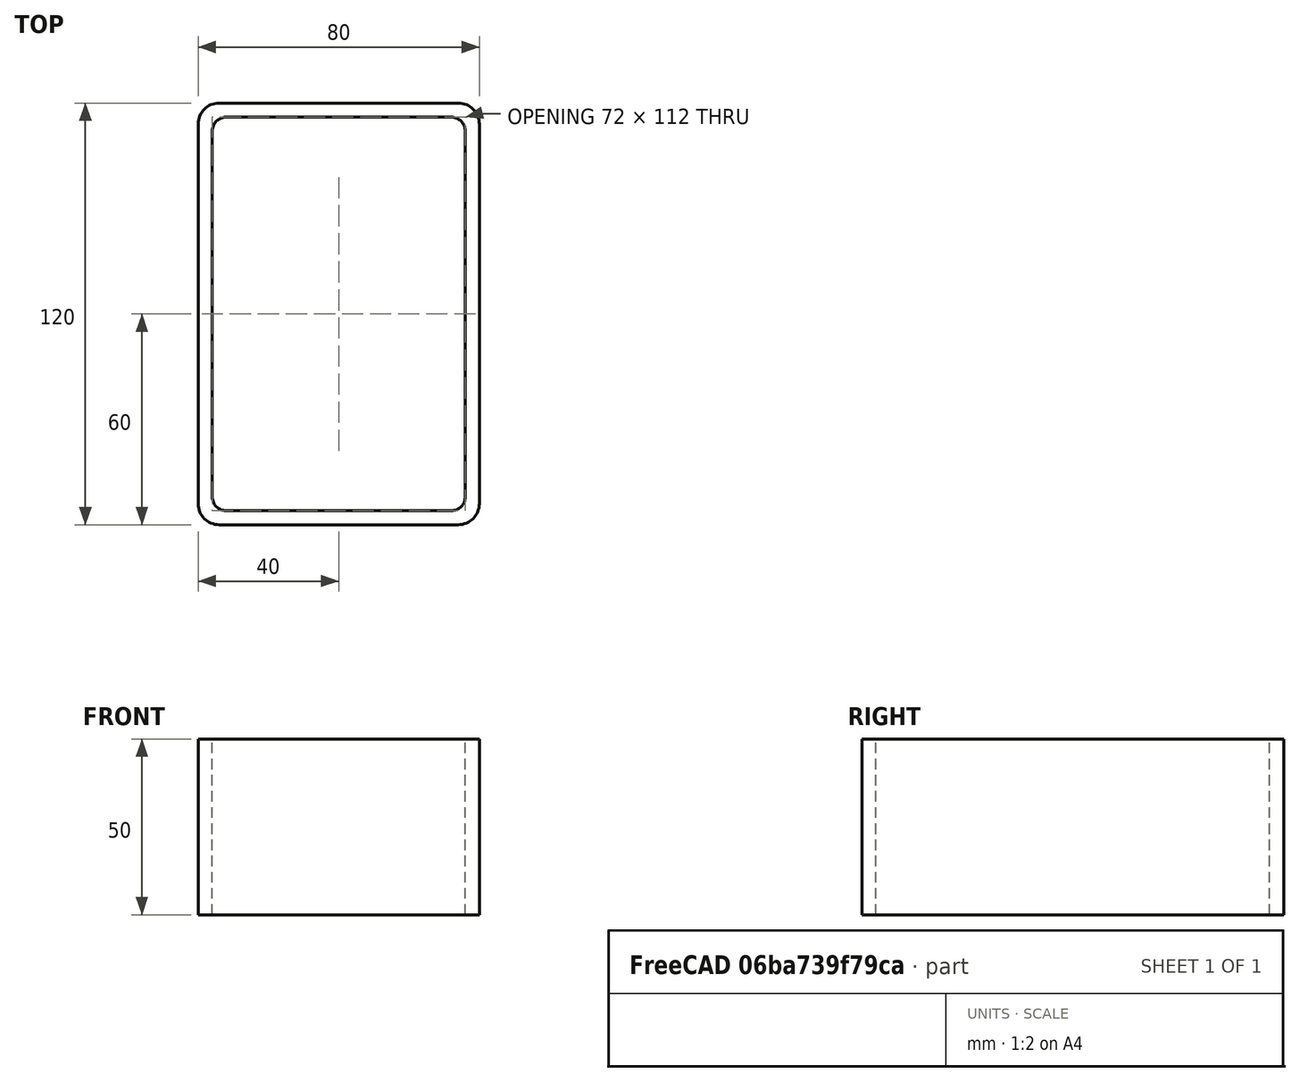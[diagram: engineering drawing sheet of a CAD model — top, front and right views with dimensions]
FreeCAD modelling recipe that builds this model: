
FCSTD DOCUMENT  (FreeCAD 0.15R4671 (Git))
Label: Rectangular hollow section 120x80x4 EN10219 S235JRH
License: All rights reserved
LicenseURL: http://en.wikipedia.org/wiki/All_rights_reserved
objects: Sketcher::SketchObject×1, Part::Extrusion×1
note: 2 computed .brp shape members not serialized (recipe doc carries the construction recipe); baked Part::Feature solids carry a one-line shape summary decoded from their .brp

FEATURE [Sketcher::SketchObject] Sketch
  sketch-geometry (16):
    g0: LineSegment StartX=-32 StartY=56 StartZ=0 EndX=32 EndY=56 EndZ=0
    g1: LineSegment StartX=36 StartY=52 StartZ=0 EndX=36 EndY=-52 EndZ=0
    g2: LineSegment StartX=32 StartY=-56 StartZ=0 EndX=-32 EndY=-56 EndZ=0
    g3: LineSegment StartX=-36 StartY=-52 StartZ=0 EndX=-36 EndY=52 EndZ=0
    g4: LineSegment StartX=-34 StartY=60 StartZ=0 EndX=34 EndY=60 EndZ=0
    g5: LineSegment StartX=40 StartY=54 StartZ=0 EndX=40 EndY=-54 EndZ=0
    g6: LineSegment StartX=34 StartY=-60 StartZ=0 EndX=-34 EndY=-60 EndZ=0
    g7: LineSegment StartX=-40 StartY=-54 StartZ=0 EndX=-40 EndY=54 EndZ=0
    g8: ArcOfCircle CenterX=-32 CenterY=52 CenterZ=0 NormalX=0 NormalY=0 NormalZ=1 Radius=4 StartAngle=1.5708 EndAngle=3.14159
    g9: ArcOfCircle CenterX=32 CenterY=52 CenterZ=0 NormalX=0 NormalY=0 NormalZ=1 Radius=4 StartAngle=0 EndAngle=1.5708
    g10: ArcOfCircle CenterX=32 CenterY=-52 CenterZ=0 NormalX=0 NormalY=0 NormalZ=1 Radius=4 StartAngle=4.71239 EndAngle=6.28319
    g11: ArcOfCircle CenterX=-32 CenterY=-52 CenterZ=0 NormalX=0 NormalY=0 NormalZ=1 Radius=4 StartAngle=3.14159 EndAngle=4.71239
    g12: ArcOfCircle CenterX=34 CenterY=54 CenterZ=0 NormalX=0 NormalY=0 NormalZ=1 Radius=6 StartAngle=0 EndAngle=1.5708
    g13: ArcOfCircle CenterX=34 CenterY=-54 CenterZ=0 NormalX=0 NormalY=0 NormalZ=1 Radius=6 StartAngle=4.71239 EndAngle=6.28319
    g14: ArcOfCircle CenterX=-34 CenterY=-54 CenterZ=0 NormalX=0 NormalY=0 NormalZ=1 Radius=6 StartAngle=3.14159 EndAngle=4.71239
    g15: ArcOfCircle CenterX=-34 CenterY=54 CenterZ=0 NormalX=0 NormalY=0 NormalZ=1 Radius=6 StartAngle=1.5708 EndAngle=3.14159
  constraints (36):
    c: Horizontal(g2)
    c: Vertical(g3)
    c: Horizontal(g6)
    c: Vertical(g7)
    c: Tangent(g3,g8) = 1.5708
    c: Tangent(g0,g8) = 1.5708
    c: Tangent(g0,g9) = 1.5708
    c: Tangent(g1,g9) = 1.5708
    c: Tangent(g1,g10) = 1.5708
    c: Tangent(g2,g10) = 1.5708
    c: Tangent(g2,g11) = 1.5708
    c: Tangent(g3,g11) = 1.5708
    c: Tangent(g4,g12) = 1.5708
    c: Tangent(g5,g12) = 1.5708
    c: Tangent(g5,g13) = 1.5708
    c: Tangent(g6,g13) = 1.5708
    c: Tangent(g6,g14) = 1.5708
    c: Tangent(g7,g14) = 1.5708
    c: Tangent(g7,g15) = 1.5708
    c: Tangent(g4,g15) = 1.5708
    c: Equal(g9,g8)
    c: Equal(g9,g11)
    c: Equal(g9,g10)
    c: Equal(g12,g15)
    c: Equal(g12,g14)
    c: Equal(g12,g13)
    c: Symmetric(g4,g6,g-1)
    c: Symmetric(g7,g5,g-2)
    c: DistanceY(g4,g6) = -120
    c: DistanceX(g7,g5) = 80
    c: Symmetric(g3,g1,g-2)
    c: Symmetric(g0,g2,g-1)
    c: DistanceY(g0,g4) = 4
    c: DistanceX(g5,g1) = -4
    c: Radius(g9) = 4
    c: Radius(g12) = 6
FEATURE [Part::Extrusion] Extrude  label="Rectangular hollow section 120x80x4 EN10219 S235JRH"
  Base = -> Sketch
  Dir = (0,0,50)
  Solid = true
